# Revit family: BEEHIVE COMBO
name_source: partatom
category: Furniture Systems
units: mm (PartAtom-declared; Revit-internal decimal feet)

## family parameters
Always vertical = Yes
Cut with Voids When Loaded = No
Part Type = Normal
Room Calculation Point = No
Round Connector Dimension = Use Diameter
Shared = No
Work Plane-Based = No

## types (1)
- BEEHIVE COMBO
    Base = <By Category>
    Description = Combo Products - BEEHIVE COMBO
    Glide = <By Category>
    Honeycomb Ottoman = F004-24x21x18
    Honeycomb Ottoman-1 Seat Fabric = <By Category>
    Honeycomb Ottoman-1 Side Fabric = <By Category>
    Honeycomb Ottoman-2 Seat Fabric = <By Category>
    Honeycomb Ottoman-2 Side Fabric = <By Category>
    Honeycomb Ottoman-3 Seat Fabric = <By Category>
    Honeycomb Ottoman-3 Side Fabric = <By Category>
    Honeycomb Ottoman-4 Seat Fabric = <By Category>
    Honeycomb Ottoman-4 Side Fabric = <By Category>
    Honeycomb Ottoman-5 Seat Fabric = <By Category>
    Honeycomb Ottoman-5 Side Fabric = <By Category>
    Honeycomb Ottoman-6 Seat Fabric = <By Category>
    Honeycomb Ottoman-6 Side Fabric = <By Category>
    Honeycomb Ottoman-7 Seat Fabric = <By Category>
    Honeycomb Ottoman-7 Side Fabric = <By Category>
    Manufacturer = FOMCORE
    Model = BEEHIVE COMBO
    URL = https://fomcore.com

## geometry (parser evidence)
native form markers: Sweep x2
no freeform markers — native parametric forms only
